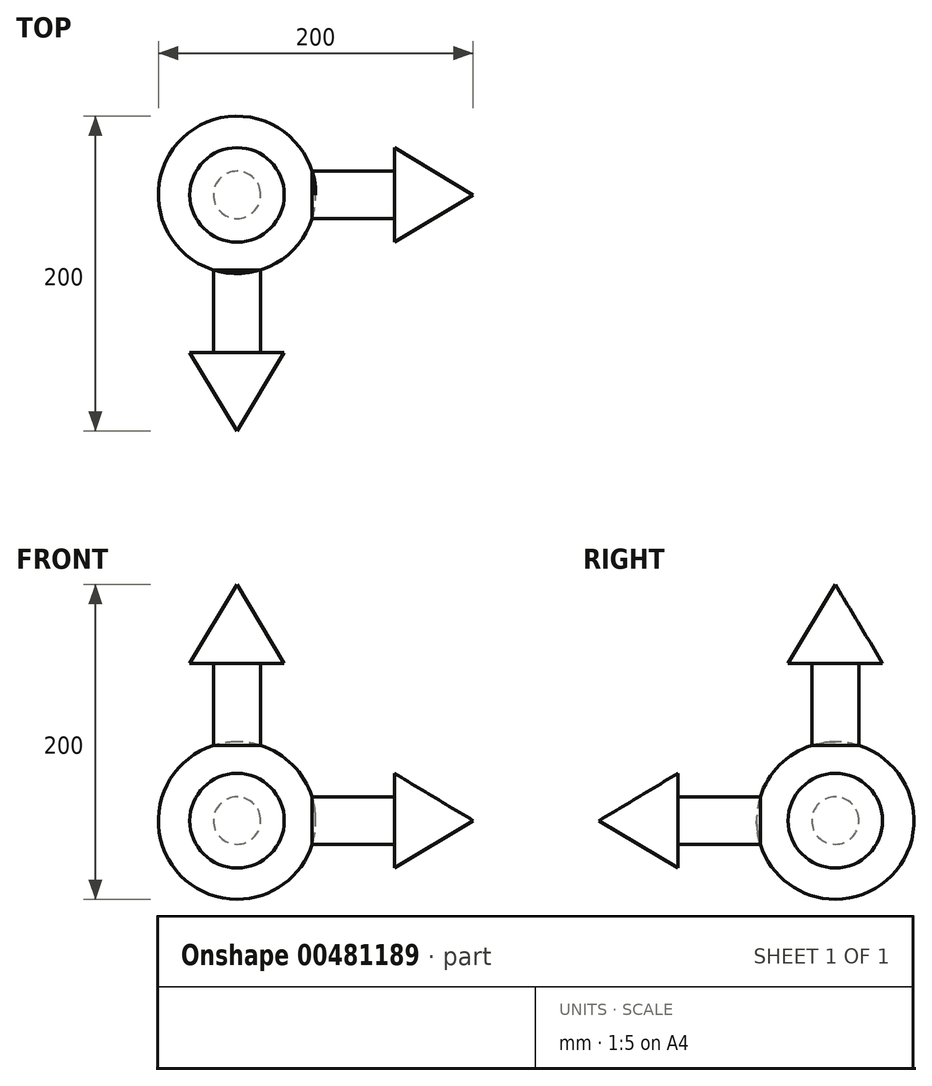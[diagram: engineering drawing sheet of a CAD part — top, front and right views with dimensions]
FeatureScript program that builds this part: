
annotation { "Feature Type Name" : "Feature", "Feature Type Description" : "" }
export const myFeature = defineFeature(function(context is Context, id is Id, definition is map)
    precondition{}
    {
        {
            var Q0;
            Q0=qCreatedBy(makeId("Front.planeOp"),FACE);
            var sketch = newSketch(context, id + "F0", { "sketchPlane" : qUnion([Q0])});
            skArc(sketch, "E0", {"start": v(0, 50) * mm, "mid": v(-50, 0) * mm, "end": v(0, -50) * mm});
            skLineSegment(sketch, "E1", {"start": v(0, 50) * mm, "end": v(0, -50) * mm});
            skSolve(sketch);
        }
        {
            var Q0;
            Q0 = qSketchRegion(id + "F0", true);
            var Q1;
            Q1=sQuery(id+"F0.wireOp",EDGE,"E1");
            revolve(context, id + "F1", {"entities" : qUnion([Q0]), "axis" : qUnion([Q1]), "revolveType" : RevolveType.FULL});
        }
        {
            var Q0;
            Q0=qCreatedBy(makeId("Front.planeOp"),FACE);
            var sketch = newSketch(context, id + "F2", { "sketchPlane" : qUnion([Q0])});
            skLineSegment(sketch, "E2", {"start": v(47.7, 15) * mm, "end": v(100, 15) * mm});
            skLineSegment(sketch, "E3", {"start": v(100, 15) * mm, "end": v(100, 30) * mm});
            skLineSegment(sketch, "E4", {"start": v(100, 30) * mm, "end": v(150, 0) * mm});
            skCircle(sketch, "E5", {"center": v(0, 0) * mm, "radius": 50 * mm});
            skLineSegment(sketch, "E6", {"start": v(150, 0) * mm, "end": v(50, 0) * mm});
            skSolve(sketch);
        }
        {
            var Q0;
            {var subQ1=sQuery(id+"F2.wireOp",EDGE,"E2");Q0=makeQuery(id+"F2.imprint","IMPRINT",FACE,{"disambiguationData":[TD([[makeQuery(id+"F2.imprint","IMPRINT",EDGE,{"derivedFrom":subQ1}),-1.0]])]});}
            var Q1;
            Q1=sQuery(id+"F2.wireOp",EDGE,"E6");
            revolve(context, id + "F3", {"entities" : qUnion([Q0]), "axis" : qUnion([Q1]), "revolveType" : RevolveType.FULL});
        }
        {
            var Q0;
            Q0=makeQuery(id+"F3.opRevolve","SWEPT_BODY",BODY,{"disambiguationData":[OSD([sQuery(id+"F2.wireOp",EDGE,"E2"),sQuery(id+"F2.wireOp",EDGE,"E3"),sQuery(id+"F2.wireOp",EDGE,"E4"),sQuery(id+"F2.wireOp",EDGE,"E5"),sQuery(id+"F2.wireOp",EDGE,"E6")])]});
            var Q1;
            Q1=sQuery(id+"F0.wireOp",EDGE,"E1");
            circularPattern(context, id + "F4", {"entities" : qUnion([Q0]), "axis" : qUnion([Q1]), "angle" : 90 * degree, "instanceCount" : 2, "equalSpace" : true});
        }
        {
            var Q0;
            Q0=qCreatedBy(makeId("Front.planeOp"),FACE);
            var sketch = newSketch(context, id + "F5", { "sketchPlane" : qUnion([Q0])});
            skLineSegment(sketch, "E7", {"start": v(-49.84, 0) * mm, "end": v(50.18, 0) * mm, "construction": true});
            skSolve(sketch);
        }
        {
            var Q0;
            Q0=makeQuery(id+"F4.opPattern","COPY",BODY,{"derivedFrom":makeQuery(id+"F3.opRevolve","SWEPT_BODY",BODY,{"disambiguationData":[OSD([sQuery(id+"F2.wireOp",EDGE,"E2"),sQuery(id+"F2.wireOp",EDGE,"E3"),sQuery(id+"F2.wireOp",EDGE,"E4"),sQuery(id+"F2.wireOp",EDGE,"E5"),sQuery(id+"F2.wireOp",EDGE,"E6")])]}),"instanceName":"1"});
            var Q1;
            Q1=sQuery(id+"F5.wireOp",EDGE,"E7");
            circularPattern(context, id + "F6", {"entities" : qUnion([Q0]), "axis" : qUnion([Q1]), "angle" : 90 * degree, "instanceCount" : 2, "oppositeDirection" : true, "equalSpace" : true});
        }
    });
